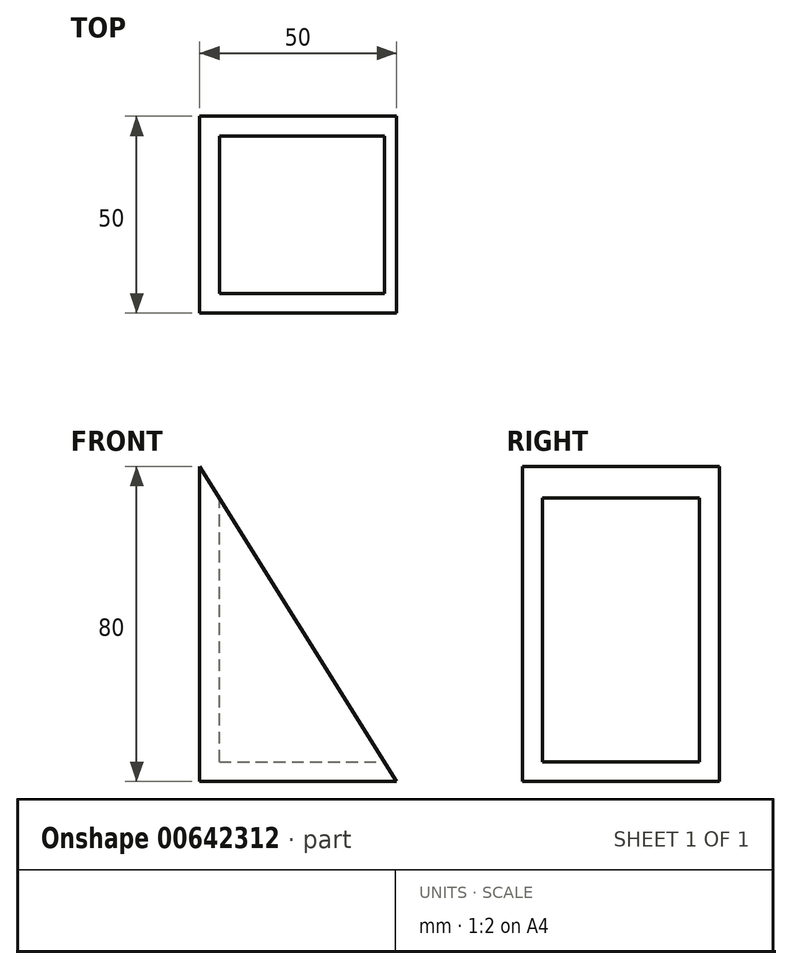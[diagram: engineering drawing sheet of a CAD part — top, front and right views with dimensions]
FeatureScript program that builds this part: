
annotation { "Feature Type Name" : "Feature", "Feature Type Description" : "" }
export const myFeature = defineFeature(function(context is Context, id is Id, definition is map)
    precondition{}
    {
        {
            var Q0;
            Q0=qCreatedBy(makeId("Front.planeOp"),FACE);
            var sketch = newSketch(context, id + "F0", { "sketchPlane" : qUnion([Q0])});
            skLineSegment(sketch, "E0", {"start": v(0, 0) * mm, "end": v(0, 80) * mm});
            skLineSegment(sketch, "E1", {"start": v(0, 80) * mm, "end": v(50, 0) * mm});
            skLineSegment(sketch, "E2", {"start": v(50, 0) * mm, "end": v(0, 0) * mm});
            skSolve(sketch);
        }
        {
            var Q0;
            Q0=makeQuery(id+"F0.imprint","IMPRINT",FACE,{"disambiguationData":[TD([[makeQuery(id+"F0.imprint","IMPRINT",EDGE,{"derivedFrom":sQuery(id+"F0.wireOp",EDGE,"E0")}),-1.0]])]});
            extrude(context, id + "F1", {"entities" : qUnion([Q0]), "depth" : 50 * mm, "offsetDistance" : 25 * mm});
        }
        {
            var Q0;
            Q0=qCreatedBy(makeId("Top.planeOp"),FACE);
            cPlane(context, id + "F2", {"entities" : qUnion([Q0]), "cplaneType" : CPlaneType.OFFSET, "offset" : 100 * mm, "width" : 150 * mm, "height" : 150 * mm});
        }
        {
            var Q0;
            Q0=qCreatedBy(id+"F2.planeOp",FACE);
            var sketch = newSketch(context, id + "F3", { "sketchPlane" : qUnion([Q0])});
            skLineSegment(sketch, "E3.bottom", {"start": v(5, -5) * mm, "end": v(50, -5) * mm});
            skLineSegment(sketch, "E3.top", {"start": v(5, -45) * mm, "end": v(50, -45) * mm});
            skLineSegment(sketch, "E3.left", {"start": v(5, -5) * mm, "end": v(5, -45) * mm});
            skLineSegment(sketch, "E3.right", {"start": v(50, -5) * mm, "end": v(50, -45) * mm});
            skPoint(sketch, "E3.middle", {"position": v(27.5, -25) * mm});
            skSolve(sketch);
        }
        {
            var Q0;
            Q0=makeQuery(id+"F3.imprint","IMPRINT",FACE,{"disambiguationData":[TD([[makeQuery(id+"F3.imprint","IMPRINT",EDGE,{"derivedFrom":sQuery(id+"F3.wireOp",EDGE,"E3.bottom")}),-1.0]])]});
            extrude(context, id + "F4", {"entities" : qUnion([Q0]), "operationType" : NewBodyOperationType.REMOVE, "oppositeDirection" : true, "depth" : 95 * mm, "offsetDistance" : 25 * mm});
        }
    });
